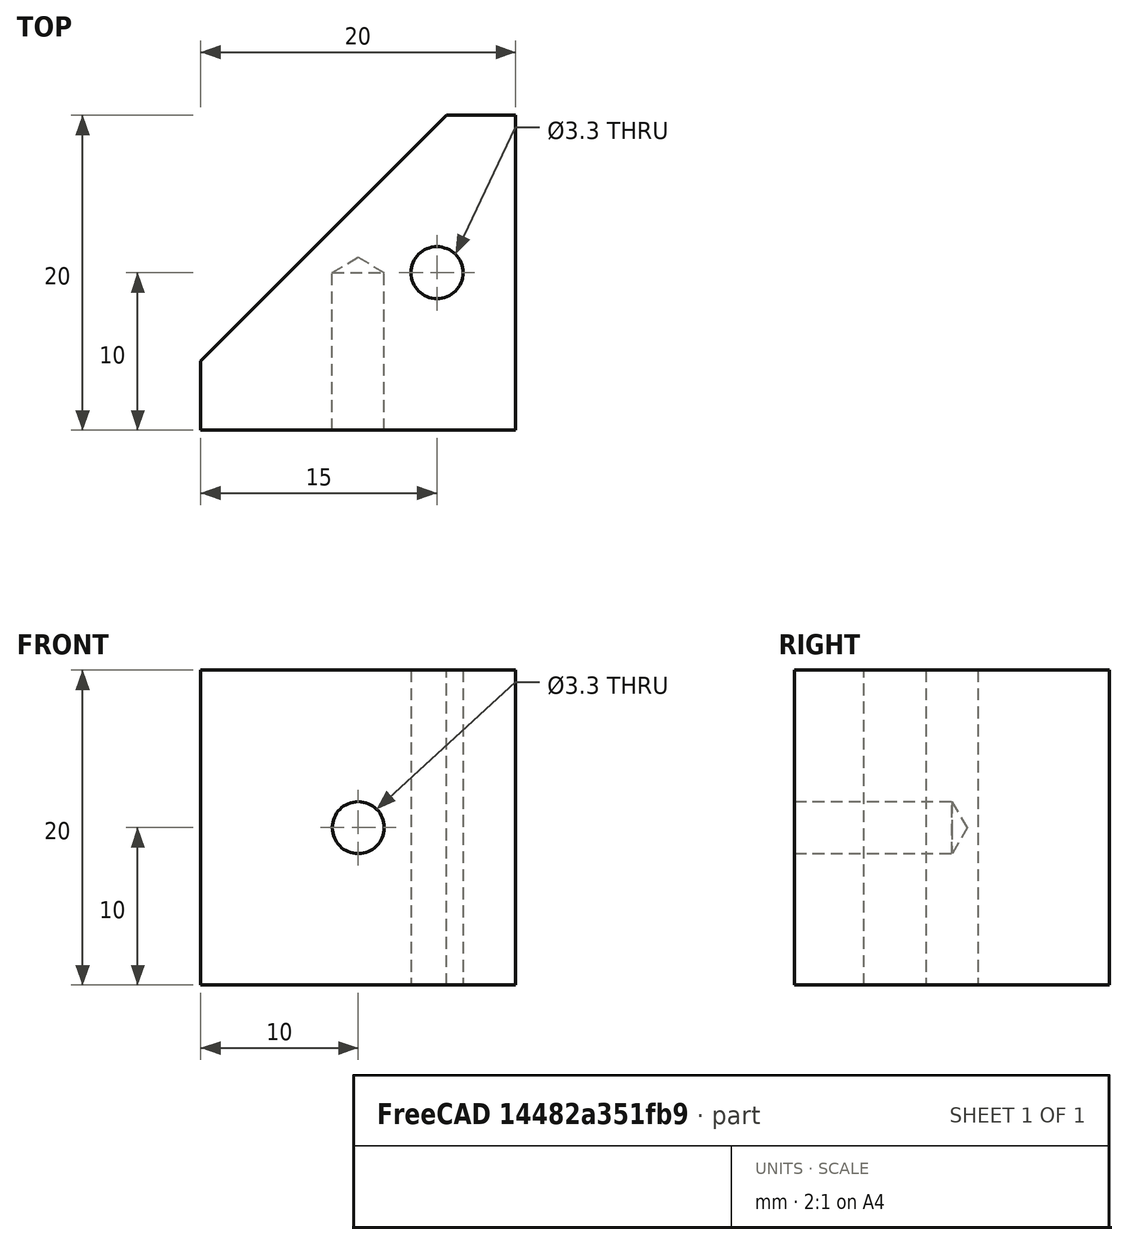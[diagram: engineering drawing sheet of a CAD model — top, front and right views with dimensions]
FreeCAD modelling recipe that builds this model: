
FCSTD DOCUMENT  (FreeCAD 1.0R39319 (Git))
Label: OCT-LBLOK-AA
License: Creative Commons Attribution 4.0
LicenseURL: https://creativecommons.org/licenses/by/4.0/
objects: TechDraw::DrawViewDimension×12, Sketcher::SketchObject×3, PartDesign::Hole×2, TechDraw::DrawProjGroupItem×2, PartDesign::Pad×1, PartDesign::Body×1, TechDraw::DrawSVGTemplate×1, TechDraw::DrawProjGroup×1, TechDraw::DrawPage×1
note: 33 computed .brp shape members not serialized (recipe doc carries the construction recipe); baked Part::Feature solids carry a one-line shape summary decoded from their .brp

FEATURE [Sketcher::SketchObject] Sketch
  ArcFitTolerance = 1e-06
  AttachmentSupport = -> [XY_Plane]
  FullyConstrained = true
  MakeInternals = false
  MapMode = 5
  sketch-geometry (5):
    g0: LineSegment StartX=-65 StartY=0 StartZ=0 EndX=-85 EndY=0 EndZ=0
    g1: LineSegment StartX=-85 StartY=0 StartZ=0 EndX=-85 EndY=4.4 EndZ=0
    g2: LineSegment StartX=-85 StartY=4.4 StartZ=0 EndX=-69.4 EndY=20 EndZ=0
    g3: LineSegment StartX=-69.4 StartY=20 StartZ=0 EndX=-65 EndY=20 EndZ=0
    g4: LineSegment StartX=-65 StartY=20 StartZ=0 EndX=-65 EndY=0 EndZ=0
  constraints (15):
    c: PointOnObject(g0,g-1)
    c: PointOnObject(g0,g-1)
    c: Coincident(g0,g1)
    c: Vertical(g1)
    c: Coincident(g1,g2)
    c: Coincident(g2,g3)
    c: Horizontal(g3)
    c: Coincident(g3,g4)
    c: Coincident(g4,g0)
    c: Vertical(g4)
    c: Angle(g1,g2) = 2.35619
    c: DistanceX(g0,g0) = 20
    c: DistanceY(g4,g4) = 20
    c: DistanceY(g1,g1) = 4.4
    c: DistanceX(g0,g-1) = 85
FEATURE [PartDesign::Pad] Pad
  Direction = (0,0,1)
  Length = 20
  Length2 = 10
  Profile = -> Sketch
  ReferenceAxis = -> Sketch [N_Axis]
  Suppressed = false
  Type = 0
FEATURE [Sketcher::SketchObject] Sketch001
  ArcFitTolerance = 1e-06
  AttachmentSupport = -> [Pad]
  FullyConstrained = true
  MakeInternals = false
  MapMode = 5
  Placement = pos=(0,0,0) rot=(1,0,0;1.5708rad)
  sketch-geometry (1):
    g0: Circle CenterX=-75 CenterY=10 CenterZ=0 NormalX=0 NormalY=0 NormalZ=1 AngleXU=0 Radius=2
  constraints (3):
    c: Distance(g0,g-1) = 10
    c: Distance(g0,g-2) = 75
    c: Diameter(g0) = 4
FEATURE [PartDesign::Hole] Hole
  BaseFeature = -> Pad
  CustomThreadClearance = 0
  Depth = 10
  DepthType = 0
  Diameter = 3.3
  DrillForDepth = false
  DrillPoint = 1
  DrillPointAngle = 118
  HoleCutCountersinkAngle = 90
  HoleCutCustomValues = false
  HoleCutDepth = 0
  HoleCutDiameter = 6.1
  HoleCutType = 0
  ModelThread = false
  Profile = -> Sketch001
  Suppressed = false
  Tapered = false
  TaperedAngle = 90
  ThreadClass = 0
  ThreadDepth = 10
  ThreadDepthType = 0
  ThreadDirection = 0
  ThreadFit = 0
  ThreadSize = 11
  ThreadType = 1
  Threaded = true
  UseCustomThreadClearance = false
FEATURE [Sketcher::SketchObject] Sketch002
  ArcFitTolerance = 1e-06
  AttachmentSupport = -> [Hole]
  FullyConstrained = true
  MakeInternals = false
  MapMode = 5
  Placement = pos=(0,0,20) rot=(0,0,1;0rad)
  sketch-geometry (1):
    g0: Circle CenterX=-70 CenterY=10 CenterZ=0 NormalX=0 NormalY=0 NormalZ=1 AngleXU=0 Radius=2
  constraints (3):
    c: Diameter(g0) = 4
    c: Distance(g0,g-1) = 10
    c: Distance(g0,g-2) = 70
FEATURE [PartDesign::Hole] Hole001
  BaseFeature = -> Hole
  CustomThreadClearance = 0
  Depth = 69.9749
  DepthType = 1
  Diameter = 3.3
  DrillForDepth = false
  DrillPoint = 1
  DrillPointAngle = 118
  HoleCutCountersinkAngle = 90
  HoleCutCustomValues = false
  HoleCutDepth = 0
  HoleCutDiameter = 6.1
  HoleCutType = 0
  ModelThread = false
  Profile = -> Sketch002
  Suppressed = false
  Tapered = false
  TaperedAngle = 90
  ThreadClass = 0
  ThreadDepth = 69.9749
  ThreadDepthType = 0
  ThreadDirection = 0
  ThreadFit = 0
  ThreadSize = 11
  ThreadType = 1
  Threaded = true
  UseCustomThreadClearance = false
FEATURE [PartDesign::Body] Body  label="lower block"
  AllowCompound = false
  Group = -> [Sketch,Pad,Sketch001,Hole,Sketch002,Hole001]
  Origin = -> Origin
  Tip = -> Hole001
FEATURE [TechDraw::DrawSVGTemplate] Template
  EditableTexts = approval_person=S. Aphelion; creator=Michael Stoll; date_of_issue=08/02/2026; document_status=In preparation; document_type=Component Drawing; drawing_number=DN; general_tolerances=ISO 2768-m; language_code=EN; part_material=Aluminium 6082 T6; responsible_department=RD; revision_index=A; scale=2 : 1; sheet_number=1 / 1; supplementary_title_1=Lower Panel Block; title=OCT-LBLOK-AA
  Height = 297
  Orientation = 1
  Template = C:/Program Files/FreeCAD 1.0/data/Mod/TechDraw/Templates/A3_Landscape_ISO5457_advanced.svg
  Width = 420
FEATURE [TechDraw::DrawProjGroupItem] View  label="Front"
  CoarseView = false
  Direction = (0,-1,0)
  Focus = 100
  HardHidden = false
  IsoCount = 0
  IsoHidden = false
  IsoVisible = false
  LockPosition = true
  Perspective = false
  Rotation = 0
  RotationVector = (1,0,0)
  Scale = 2
  ScaleType = 2
  ScrubCount = 1
  SeamHidden = false
  SeamVisible = false
  SmoothHidden = false
  SmoothVisible = true
  Source = -> [Body]
  Type = 0
  X = 0
  XDirection = (1,0,0)
  Y = 0
FEATURE [TechDraw::DrawProjGroupItem] ProjItem  label="Top"
  CoarseView = false
  Direction = (0,0,1)
  Focus = 100
  HardHidden = false
  IsoCount = 0
  IsoHidden = false
  IsoVisible = false
  LockPosition = false
  Perspective = false
  Rotation = 0
  RotationVector = (1,0,0)
  Scale = 2
  ScaleType = 0
  ScrubCount = 1
  SeamHidden = false
  SeamVisible = false
  SmoothHidden = false
  SmoothVisible = true
  Source = -> [Body]
  Type = 4
  X = 0
  XDirection = (1,0,0)
  Y = 90
FEATURE [TechDraw::DrawProjGroup] ProjGroup
  Anchor = -> View
  AutoDistribute = true
  LockPosition = false
  ProjectionType = 1
  Rotation = 0
  Scale = 2
  ScaleType = 0
  Source = -> [Body]
  Views = -> [View,ProjItem]
  X = 187.859
  Y = 112.499
  spacingX = 15
  spacingY = 50
FEATURE [TechDraw::DrawViewDimension] Dimension
  AngleOverride = false
  Arbitrary = false
  ArbitraryTolerances = false
  BoxCorners = (2) [(-20,-20,0),(20,20,0)]
  EqualTolerance = true
  ExtensionAngle = 0
  FormatSpec = %.1f
  FormatSpecOverTolerance = %+.1f
  FormatSpecUnderTolerance = %+.1f
  Inverted = false
  LineAngle = 0
  LockPosition = false
  MeasureType = 1
  OverTolerance = 0
  References2D = -> [View]
  Rotation = 0
  Scale = 2
  ScaleType = 0
  TheoreticalExact = false
  Type = 2
  UnderTolerance = 0
  X = 40.7845
  Y = 0
FEATURE [TechDraw::DrawViewDimension] Dimension001
  AngleOverride = false
  Arbitrary = false
  ArbitraryTolerances = false
  BoxCorners = (2) [(-20,-20,0),(20,20,0)]
  EqualTolerance = true
  ExtensionAngle = 0
  FormatSpec = %.1f
  FormatSpecOverTolerance = %+.1f
  FormatSpecUnderTolerance = %+.1f
  Inverted = false
  LineAngle = 0
  LockPosition = false
  MeasureType = 1
  OverTolerance = 0
  References2D = -> [View]
  Rotation = 0
  Scale = 2
  ScaleType = 0
  TheoreticalExact = false
  Type = 1
  UnderTolerance = 0
  X = 0
  Y = -36.0087
FEATURE [TechDraw::DrawViewDimension] Dimension002
  AngleOverride = false
  Arbitrary = false
  ArbitraryTolerances = false
  BoxCorners = (2) [(-20,-20,0),(20,20,0)]
  EqualTolerance = true
  ExtensionAngle = 0
  FormatSpec = %.1f
  FormatSpecOverTolerance = %+.1f
  FormatSpecUnderTolerance = %+.1f
  Inverted = false
  LineAngle = 0
  LockPosition = false
  MeasureType = 1
  OverTolerance = 0
  References2D = -> [View]
  Rotation = 0
  Scale = 2
  ScaleType = 0
  TheoreticalExact = false
  Type = 0
  UnderTolerance = 0
  X = -46.1057
  Y = -10
FEATURE [TechDraw::DrawViewDimension] Dimension003
  AngleOverride = false
  Arbitrary = false
  ArbitraryTolerances = false
  BoxCorners = (2) [(-20,-20,0),(20,20,0)]
  EqualTolerance = true
  ExtensionAngle = 0
  FormatSpec = %.1f
  FormatSpecOverTolerance = %+.1f
  FormatSpecUnderTolerance = %+.1f
  Inverted = false
  LineAngle = 0
  LockPosition = false
  MeasureType = 1
  OverTolerance = 0
  References2D = -> [View]
  Rotation = 0
  Scale = 2
  ScaleType = 0
  TheoreticalExact = false
  Type = 0
  UnderTolerance = 0
  X = 10
  Y = 39.2356
FEATURE [TechDraw::DrawViewDimension] Dimension004
  AngleOverride = false
  Arbitrary = false
  ArbitraryTolerances = false
  BoxCorners = (2) [(-20,-20,0),(20,20,0)]
  EqualTolerance = true
  ExtensionAngle = 0
  FormatSpec = %.1f
  FormatSpecOverTolerance = %+.1f
  FormatSpecUnderTolerance = %+.1f
  Inverted = false
  LineAngle = 0
  LockPosition = false
  MeasureType = 1
  OverTolerance = 0
  References2D = -> [ProjItem]
  Rotation = 0
  Scale = 2
  ScaleType = 0
  TheoreticalExact = false
  Type = 2
  UnderTolerance = 0
  X = 42.8039
  Y = 0
FEATURE [TechDraw::DrawViewDimension] Dimension005
  AngleOverride = false
  Arbitrary = false
  ArbitraryTolerances = false
  BoxCorners = (2) [(-20,-20,0),(20,20,0)]
  EqualTolerance = true
  ExtensionAngle = 0
  FormatSpec = %.1f
  FormatSpecOverTolerance = %+.1f
  FormatSpecUnderTolerance = %+.1f
  Inverted = false
  LineAngle = 0
  LockPosition = false
  MeasureType = 1
  OverTolerance = 0
  References2D = -> [ProjItem]
  Rotation = 0
  Scale = 2
  ScaleType = 0
  TheoreticalExact = false
  Type = 2
  UnderTolerance = 0
  X = -48.6533
  Y = -15.6
FEATURE [TechDraw::DrawViewDimension] Dimension006
  AngleOverride = false
  Arbitrary = false
  ArbitraryTolerances = false
  BoxCorners = (2) [(-20,-20,0),(20,20,0)]
  EqualTolerance = true
  ExtensionAngle = 0
  FormatSpec = %.1f
  FormatSpecOverTolerance = %+.1f
  FormatSpecUnderTolerance = %+.1f
  Inverted = false
  LineAngle = 0
  LockPosition = false
  MeasureType = 1
  OverTolerance = 0
  References2D = -> [ProjItem]
  Rotation = 0
  Scale = 2
  ScaleType = 0
  TheoreticalExact = false
  Type = 0
  UnderTolerance = 0
  X = 28.9686
  Y = -10
FEATURE [TechDraw::DrawViewDimension] Dimension007
  AngleOverride = false
  Arbitrary = false
  ArbitraryTolerances = false
  BoxCorners = (2) [(-20,-20,0),(20,20,0)]
  EqualTolerance = true
  ExtensionAngle = 0
  FormatSpec = %.1f
  FormatSpecOverTolerance = %+.1f
  FormatSpecUnderTolerance = %+.1f
  Inverted = false
  LineAngle = 0
  LockPosition = false
  MeasureType = 1
  OverTolerance = 0
  References2D = -> [ProjItem]
  Rotation = 0
  Scale = 2
  ScaleType = 0
  TheoreticalExact = false
  Type = 0
  UnderTolerance = 0
  X = 15
  Y = 38.1072
FEATURE [TechDraw::DrawViewDimension] Dimension008
  AngleOverride = false
  Arbitrary = false
  ArbitraryTolerances = false
  BoxCorners = (2) [(-20,-20,0),(20,20,0)]
  EqualTolerance = true
  ExtensionAngle = 0
  FormatSpec = %.1f
  FormatSpecOverTolerance = %+.1f
  FormatSpecUnderTolerance = %+.1f
  Inverted = false
  LineAngle = 0
  LockPosition = false
  MeasureType = 1
  OverTolerance = 0
  References2D = -> [ProjItem]
  Rotation = 0
  Scale = 2
  ScaleType = 0
  TheoreticalExact = false
  Type = 1
  UnderTolerance = 0
  X = -11.6369
  Y = -10.1707
FEATURE [TechDraw::DrawViewDimension] Dimension009
  AngleOverride = false
  Arbitrary = false
  ArbitraryTolerances = false
  BoxCorners = (2) [(-20,-20,0),(20,20,0)]
  EqualTolerance = true
  ExtensionAngle = 0
  FormatSpec = %.1f
  FormatSpecOverTolerance = %+.1f
  FormatSpecUnderTolerance = %+.1f
  Inverted = false
  LineAngle = 0
  LockPosition = false
  MeasureType = 1
  OverTolerance = 0
  References2D = -> [ProjItem]
  Rotation = 0
  Scale = 2
  ScaleType = 0
  TheoreticalExact = false
  Type = 6
  UnderTolerance = 0
  X = 67.5859
  Y = 30.1305
FEATURE [TechDraw::DrawViewDimension] Dimension010
  AngleOverride = false
  Arbitrary = false
  ArbitraryTolerances = false
  BoxCorners = (2) [(-20,-20,0),(20,20,0)]
  EqualTolerance = true
  ExtensionAngle = 0
  FormatSpec = ⌀%.1f
  FormatSpecOverTolerance = %+.1f
  FormatSpecUnderTolerance = %+.1f
  Inverted = false
  LineAngle = 0
  LockPosition = false
  MeasureType = 1
  OverTolerance = 0
  References2D = -> [ProjItem]
  Rotation = 0
  Scale = 2
  ScaleType = 0
  TheoreticalExact = false
  Type = 5
  UnderTolerance = 0
  X = -26.9107
  Y = 20.7938
FEATURE [TechDraw::DrawViewDimension] Dimension011
  AngleOverride = false
  Arbitrary = false
  ArbitraryTolerances = false
  BoxCorners = (2) [(-20,-20,0),(20,20,0)]
  EqualTolerance = true
  ExtensionAngle = 0
  FormatSpec = ⌀%.1f
  FormatSpecOverTolerance = %+.1f
  FormatSpecUnderTolerance = %+.1f
  Inverted = false
  LineAngle = 0
  LockPosition = false
  MeasureType = 1
  OverTolerance = 0
  References2D = -> [View]
  Rotation = 0
  Scale = 2
  ScaleType = 0
  TheoreticalExact = false
  Type = 5
  UnderTolerance = 0
  X = -40.3396
  Y = 24.9886
FEATURE [TechDraw::DrawPage] Page
  KeepUpdated = true
  NextBalloonIndex = 1
  ProjectionType = 1
  Scale = 2
  Template = -> Template
  Views = -> [ProjGroup,Dimension,Dimension001,Dimension002,Dimension003,Dimension004,Dimension005,Dimension006,Dimension007,Dimension008,Dimension009,Dimension010,Dimension011]
